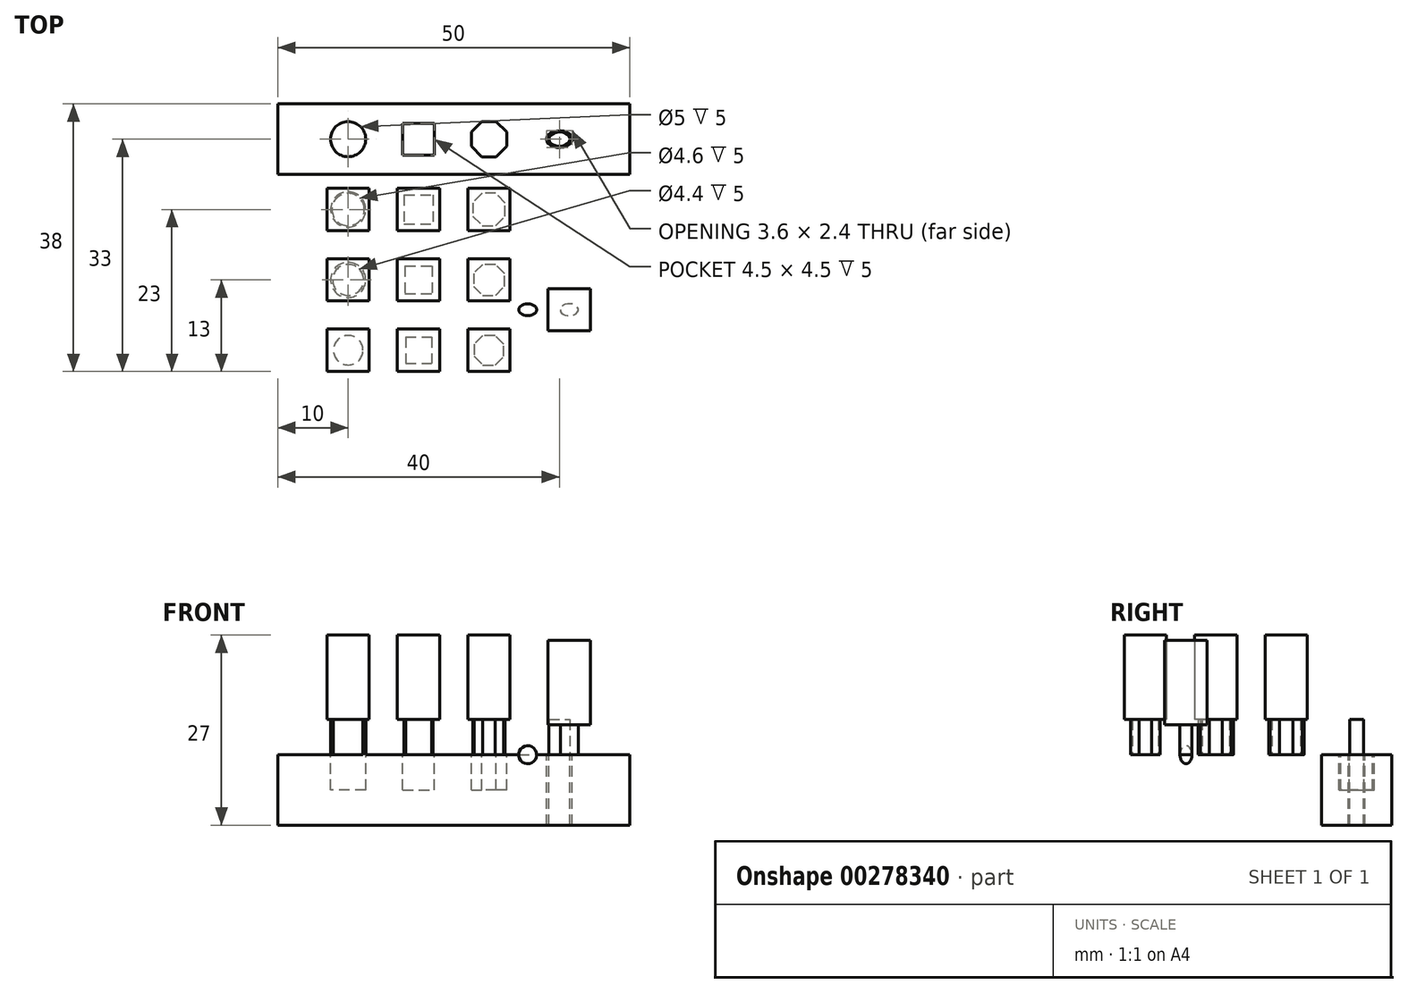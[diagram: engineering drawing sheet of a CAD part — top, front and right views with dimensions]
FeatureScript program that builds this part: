
annotation { "Feature Type Name" : "Feature", "Feature Type Description" : "" }
export const myFeature = defineFeature(function(context is Context, id is Id, definition is map)
    precondition{}
    {
        {
            var Q0;
            Q0=qCreatedBy(makeId("Top.planeOp"),FACE);
            var sketch = newSketch(context, id + "F0", { "sketchPlane" : qUnion([Q0])});
            skLineSegment(sketch, "E0.bottom", {"start": v(0, 0) * mm, "end": v(50, 0) * mm});
            skLineSegment(sketch, "E0.top", {"start": v(0, 10) * mm, "end": v(50, 10) * mm});
            skLineSegment(sketch, "E0.left", {"start": v(0, 0) * mm, "end": v(0, 10) * mm});
            skLineSegment(sketch, "E0.right", {"start": v(50, 0) * mm, "end": v(50, 10) * mm});
            skCircle(sketch, "E1", {"center": v(10, 5) * mm, "radius": 2.5 * mm});
            skPoint(sketch, "E1.centerSnap0", {"position": v(0, 5) * mm});
            skLineSegment(sketch, "E2.bottom", {"start": v(17.75, 2.75) * mm, "end": v(22.25, 2.75) * mm});
            skLineSegment(sketch, "E2.top", {"start": v(17.75, 7.25) * mm, "end": v(22.25, 7.25) * mm});
            skLineSegment(sketch, "E2.left", {"start": v(17.75, 2.75) * mm, "end": v(17.75, 7.25) * mm});
            skLineSegment(sketch, "E2.right", {"start": v(22.25, 2.75) * mm, "end": v(22.25, 7.25) * mm});
            skPoint(sketch, "E2.middle", {"position": v(20, 5) * mm});
            skCircle(sketch, "E3.cCircle", {"center": v(30, 5) * mm, "radius": 2.5 * mm, "construction": true});
            skPoint(sketch, "E3.cCircle.centerSnap0", {"position": v(22.25, 5) * mm});
            skLineSegment(sketch, "E3.0", {"start": v(27.5, 6.04) * mm, "end": v(28.96, 7.5) * mm});
            skLineSegment(sketch, "E3.1", {"start": v(28.96, 7.5) * mm, "end": v(31.04, 7.5) * mm});
            skLineSegment(sketch, "E3.2", {"start": v(31.04, 7.5) * mm, "end": v(32.5, 6.04) * mm});
            skLineSegment(sketch, "E3.3", {"start": v(32.5, 6.04) * mm, "end": v(32.5, 3.96) * mm});
            skLineSegment(sketch, "E3.4", {"start": v(32.5, 3.96) * mm, "end": v(31.04, 2.5) * mm});
            skLineSegment(sketch, "E3.5", {"start": v(31.04, 2.5) * mm, "end": v(28.96, 2.5) * mm});
            skLineSegment(sketch, "E3.6", {"start": v(28.96, 2.5) * mm, "end": v(27.5, 3.96) * mm});
            skLineSegment(sketch, "E3.7", {"start": v(27.5, 3.96) * mm, "end": v(27.5, 6.04) * mm});
            skPoint(sketch, "E3.0.midPoint", {"position": v(28.23, 6.77) * mm});
            skLineSegment(sketch, "E4", {"start": v(40, 2.6) * mm, "end": v(40, 7.41) * mm});
            skCircle(sketch, "E5.MirrorC", {"center": v(10, -5) * mm, "radius": 2.5 * mm});
            skLineSegment(sketch, "E6.MirrorCS", {"start": v(17.75, -2.75) * mm, "end": v(17.75, -7.25) * mm});
            skLineSegment(sketch, "E7.MirrorCS", {"start": v(17.75, -7.25) * mm, "end": v(22.25, -7.25) * mm});
            skLineSegment(sketch, "E8.MirrorCS", {"start": v(22.25, -2.75) * mm, "end": v(22.25, -7.25) * mm});
            skLineSegment(sketch, "E9.MirrorCS", {"start": v(17.75, -2.75) * mm, "end": v(22.25, -2.75) * mm});
            skLineSegment(sketch, "E10.MirrorCS", {"start": v(27.5, -6.04) * mm, "end": v(28.96, -7.5) * mm});
            skLineSegment(sketch, "E11.MirrorCS", {"start": v(28.96, -7.5) * mm, "end": v(31.04, -7.5) * mm});
            skLineSegment(sketch, "E12.MirrorCS", {"start": v(31.04, -7.5) * mm, "end": v(32.5, -6.04) * mm});
            skLineSegment(sketch, "E13.MirrorCS", {"start": v(32.5, -6.04) * mm, "end": v(32.5, -3.96) * mm});
            skLineSegment(sketch, "E14.MirrorCS", {"start": v(32.5, -3.96) * mm, "end": v(31.04, -2.5) * mm});
            skLineSegment(sketch, "E15.MirrorCS", {"start": v(31.04, -2.5) * mm, "end": v(28.96, -2.5) * mm});
            skLineSegment(sketch, "E16.MirrorCS", {"start": v(28.96, -2.5) * mm, "end": v(27.5, -3.96) * mm});
            skLineSegment(sketch, "E17.MirrorCS", {"start": v(27.5, -3.96) * mm, "end": v(27.5, -6.04) * mm});
            skLineSegment(sketch, "E18.0.1.0", {"start": v(31.04, -17.5) * mm, "end": v(32.5, -16.04) * mm});
            skLineSegment(sketch, "E18.0.1.1", {"start": v(17.75, -12.75) * mm, "end": v(17.75, -17.25) * mm});
            skLineSegment(sketch, "E18.0.1.2", {"start": v(17.75, -12.75) * mm, "end": v(22.25, -12.75) * mm});
            skLineSegment(sketch, "E18.0.1.3", {"start": v(27.5, -16.04) * mm, "end": v(28.96, -17.5) * mm});
            skCircle(sketch, "E18.0.1.5", {"center": v(10, -15) * mm, "radius": 2.5 * mm});
            skLineSegment(sketch, "E18.0.1.6", {"start": v(17.75, -17.25) * mm, "end": v(22.25, -17.25) * mm});
            skLineSegment(sketch, "E18.0.1.7", {"start": v(27.5, -13.96) * mm, "end": v(27.5, -16.04) * mm});
            skLineSegment(sketch, "E18.0.1.8", {"start": v(22.25, -12.75) * mm, "end": v(22.25, -17.25) * mm});
            skLineSegment(sketch, "E18.0.1.9", {"start": v(28.96, -17.5) * mm, "end": v(31.04, -17.5) * mm});
            skLineSegment(sketch, "E18.0.1.10", {"start": v(32.5, -16.04) * mm, "end": v(32.5, -13.96) * mm});
            skLineSegment(sketch, "E18.0.1.11", {"start": v(31.04, -12.5) * mm, "end": v(28.96, -12.5) * mm});
            skLineSegment(sketch, "E18.0.1.12", {"start": v(28.96, -12.5) * mm, "end": v(27.5, -13.96) * mm});
            skLineSegment(sketch, "E18.0.1.13", {"start": v(32.5, -13.96) * mm, "end": v(31.04, -12.5) * mm});
            skLineSegment(sketch, "E18.0.2.0", {"start": v(31.04, -27.5) * mm, "end": v(32.5, -26.04) * mm});
            skLineSegment(sketch, "E18.0.2.1", {"start": v(17.75, -22.75) * mm, "end": v(17.75, -27.25) * mm});
            skLineSegment(sketch, "E18.0.2.2", {"start": v(17.75, -22.75) * mm, "end": v(22.25, -22.75) * mm});
            skLineSegment(sketch, "E18.0.2.3", {"start": v(27.5, -26.04) * mm, "end": v(28.96, -27.5) * mm});
            skCircle(sketch, "E18.0.2.5", {"center": v(10, -25) * mm, "radius": 2.5 * mm});
            skLineSegment(sketch, "E18.0.2.6", {"start": v(17.75, -27.25) * mm, "end": v(22.25, -27.25) * mm});
            skLineSegment(sketch, "E18.0.2.7", {"start": v(27.5, -23.96) * mm, "end": v(27.5, -26.04) * mm});
            skLineSegment(sketch, "E18.0.2.8", {"start": v(22.25, -22.75) * mm, "end": v(22.25, -27.25) * mm});
            skLineSegment(sketch, "E18.0.2.9", {"start": v(28.96, -27.5) * mm, "end": v(31.04, -27.5) * mm});
            skLineSegment(sketch, "E18.0.2.10", {"start": v(32.5, -26.04) * mm, "end": v(32.5, -23.96) * mm});
            skLineSegment(sketch, "E18.0.2.11", {"start": v(31.04, -22.5) * mm, "end": v(28.96, -22.5) * mm});
            skLineSegment(sketch, "E18.0.2.12", {"start": v(28.96, -22.5) * mm, "end": v(27.5, -23.96) * mm});
            skLineSegment(sketch, "E18.0.2.13", {"start": v(32.5, -23.96) * mm, "end": v(31.04, -22.5) * mm});
            skCircle(sketch, "E19.0", {"center": v(10, -5) * mm, "radius": 2.3 * mm});
            skCircle(sketch, "E20.0", {"center": v(10, -15) * mm, "radius": 2.2 * mm});
            skCircle(sketch, "E21.0", {"center": v(10, -25) * mm, "radius": 2.1 * mm});
            skLineSegment(sketch, "E22.0", {"start": v(17.95, -2.95) * mm, "end": v(22.05, -2.95) * mm});
            skLineSegment(sketch, "E22.1", {"start": v(17.95, -2.95) * mm, "end": v(17.95, -7.05) * mm});
            skLineSegment(sketch, "E22.2", {"start": v(17.95, -7.05) * mm, "end": v(22.05, -7.05) * mm});
            skLineSegment(sketch, "E22.3", {"start": v(22.05, -2.95) * mm, "end": v(22.05, -7.05) * mm});
            skLineSegment(sketch, "E23.0", {"start": v(18.05, -13.05) * mm, "end": v(18.05, -16.95) * mm});
            skLineSegment(sketch, "E23.1", {"start": v(18.05, -13.05) * mm, "end": v(21.95, -13.05) * mm});
            skLineSegment(sketch, "E23.2", {"start": v(21.95, -13.05) * mm, "end": v(21.95, -16.95) * mm});
            skLineSegment(sketch, "E23.3", {"start": v(18.05, -16.95) * mm, "end": v(21.95, -16.95) * mm});
            skLineSegment(sketch, "E24.0", {"start": v(18.15, -23.15) * mm, "end": v(18.15, -26.85) * mm});
            skLineSegment(sketch, "E24.1", {"start": v(18.15, -23.15) * mm, "end": v(21.85, -23.15) * mm});
            skLineSegment(sketch, "E24.2", {"start": v(21.85, -23.15) * mm, "end": v(21.85, -26.85) * mm});
            skLineSegment(sketch, "E24.3", {"start": v(18.15, -26.85) * mm, "end": v(21.85, -26.85) * mm});
            skLineSegment(sketch, "E25.0", {"start": v(29.05, -7.3) * mm, "end": v(30.95, -7.3) * mm});
            skLineSegment(sketch, "E25.1", {"start": v(27.7, -5.95) * mm, "end": v(29.05, -7.3) * mm});
            skLineSegment(sketch, "E25.2", {"start": v(30.95, -7.3) * mm, "end": v(32.3, -5.95) * mm});
            skLineSegment(sketch, "E25.3", {"start": v(27.7, -4.05) * mm, "end": v(27.7, -5.95) * mm});
            skLineSegment(sketch, "E25.4", {"start": v(32.3, -5.95) * mm, "end": v(32.3, -4.05) * mm});
            skLineSegment(sketch, "E25.5", {"start": v(32.3, -4.05) * mm, "end": v(30.95, -2.7) * mm});
            skLineSegment(sketch, "E25.6", {"start": v(30.95, -2.7) * mm, "end": v(29.05, -2.7) * mm});
            skLineSegment(sketch, "E25.7", {"start": v(29.05, -2.7) * mm, "end": v(27.7, -4.05) * mm});
            skLineSegment(sketch, "E26.0", {"start": v(32.1, -25.87) * mm, "end": v(32.1, -24.13) * mm});
            skLineSegment(sketch, "E26.1", {"start": v(30.87, -27.1) * mm, "end": v(32.1, -25.87) * mm});
            skLineSegment(sketch, "E26.2", {"start": v(32.1, -24.13) * mm, "end": v(30.87, -22.9) * mm});
            skLineSegment(sketch, "E26.3", {"start": v(29.13, -27.1) * mm, "end": v(30.87, -27.1) * mm});
            skLineSegment(sketch, "E26.4", {"start": v(30.87, -22.9) * mm, "end": v(29.13, -22.9) * mm});
            skLineSegment(sketch, "E26.5", {"start": v(29.13, -22.9) * mm, "end": v(27.9, -24.13) * mm});
            skLineSegment(sketch, "E26.6", {"start": v(27.9, -24.13) * mm, "end": v(27.9, -25.87) * mm});
            skLineSegment(sketch, "E26.7", {"start": v(27.9, -25.87) * mm, "end": v(29.13, -27.1) * mm});
            skLineSegment(sketch, "E27.0", {"start": v(29.09, -12.8) * mm, "end": v(27.8, -14.09) * mm});
            skLineSegment(sketch, "E27.1", {"start": v(30.91, -12.8) * mm, "end": v(29.09, -12.8) * mm});
            skLineSegment(sketch, "E27.2", {"start": v(27.8, -14.09) * mm, "end": v(27.8, -15.91) * mm});
            skLineSegment(sketch, "E27.3", {"start": v(32.2, -14.09) * mm, "end": v(30.91, -12.8) * mm});
            skLineSegment(sketch, "E27.4", {"start": v(27.8, -15.91) * mm, "end": v(29.09, -17.2) * mm});
            skLineSegment(sketch, "E27.5", {"start": v(29.09, -17.2) * mm, "end": v(30.91, -17.2) * mm});
            skLineSegment(sketch, "E27.6", {"start": v(30.91, -17.2) * mm, "end": v(32.2, -15.91) * mm});
            skLineSegment(sketch, "E27.7", {"start": v(32.2, -15.91) * mm, "end": v(32.2, -14.09) * mm});
            skEllipse(sketch, "E28", {"center": v(40, 5) * mm, "majorRadius": 1.8 * mm, "minorRadius": 1.2 * mm, "majorAxis": v(-1, 0)});
            skPoint(sketch, "E28.centerSnap0", {"position": v(32.5, 5) * mm});
            skEllipse(sketch, "E29", {"center": v(40, 5) * mm, "majorRadius": 1.5 * mm, "minorRadius": 1 * mm, "majorAxis": v(-1, 0)});
            skSolve(sketch);
        }
        {
            var Q0;
            Q0=makeQuery(id+"F0.imprint","IMPRINT",FACE,{"disambiguationData":[TD([[makeQuery(id+"F0.imprint","IMPRINT",EDGE,{"derivedFrom":sQuery(id+"F0.wireOp",EDGE,"E0.bottom")}),1.0]])]});
            var Q1;
            Q1=makeQuery(id+"F0.imprint","IMPRINT",FACE,{"disambiguationData":[TD([[makeQuery(id+"F0.imprint","IMPRINT",EDGE,{"derivedFrom":sQuery(id+"F0.wireOp",EDGE,"E1")}),1.0]])]});
            var Q2;
            Q2=makeQuery(id+"F0.imprint","IMPRINT",FACE,{"disambiguationData":[TD([[makeQuery(id+"F0.imprint","IMPRINT",EDGE,{"derivedFrom":sQuery(id+"F0.wireOp",EDGE,"E2.bottom")}),1.0]])]});
            var Q3;
            Q3=makeQuery(id+"F0.imprint","IMPRINT",FACE,{"disambiguationData":[TD([[makeQuery(id+"F0.imprint","IMPRINT",EDGE,{"derivedFrom":sQuery(id+"F0.wireOp",EDGE,"E3.0")}),-1.0]])]});
            var Q4;
            {var subQ0=sQuery(id+"F0.wireOp",EDGE,"E4");var subQ1=sQuery(id+"F0.wireOp",EDGE,"KZuQSlj7-sCAI-CJ17-El7u-51rF61ip7YGT");var subQ2=makeQuery(id+"F0.imprint","INTERSECT",VERTEX,{"disambiguationData":[OD(0.0)],"derivedFrom":[subQ1,subQ0]});Q4=makeQuery(id+"F0.imprint","IMPRINT",FACE,{"disambiguationData":[TD([[makeQuery(id+"F0.imprint","IMPRINT",EDGE,{"disambiguationData":[TD([[subQ2,-1.0]])],"derivedFrom":subQ1}),1.0]])]});}
            var Q5;
            {var subQ0=sQuery(id+"F0.wireOp",EDGE,"E4");var subQ1=sQuery(id+"F0.wireOp",EDGE,"KZuQSlj7-sCAI-CJ17-El7u-51rF61ip7YGT");var subQ2=makeQuery(id+"F0.imprint","INTERSECT",VERTEX,{"disambiguationData":[OD(0.0)],"derivedFrom":[subQ1,subQ0]});Q5=makeQuery(id+"F0.imprint","IMPRINT",FACE,{"disambiguationData":[TD([[makeQuery(id+"F0.imprint","IMPRINT",EDGE,{"disambiguationData":[TD([[subQ2,1.0]])],"derivedFrom":subQ1}),-1.0]])]});}
            var Q6;
            {var subQ0=sQuery(id+"F0.wireOp",EDGE,"E4");var subQ1=sQuery(id+"F0.wireOp",EDGE,"KZuQSlj7-sCAI-CJ17-El7u-51rF61ip7YGT");var subQ2=makeQuery(id+"F0.imprint","INTERSECT",VERTEX,{"disambiguationData":[OD(0.0)],"derivedFrom":[subQ1,subQ0]});Q6=makeQuery(id+"F0.imprint","IMPRINT",FACE,{"disambiguationData":[TD([[makeQuery(id+"F0.imprint","IMPRINT",EDGE,{"disambiguationData":[TD([[subQ2,-1.0]])],"derivedFrom":subQ1}),-1.0]])]});}
            var Q7;
            {var subQ0=sQuery(id+"F0.wireOp",EDGE,"E4");var subQ1=sQuery(id+"F0.wireOp",EDGE,"KZuQSlj7-sCAI-CJ17-El7u-51rF61ip7YGT");var subQ2=makeQuery(id+"F0.imprint","INTERSECT",VERTEX,{"disambiguationData":[OD(0.0)],"derivedFrom":[subQ1,subQ0]});Q7=makeQuery(id+"F0.imprint","IMPRINT",FACE,{"disambiguationData":[TD([[makeQuery(id+"F0.imprint","IMPRINT",EDGE,{"disambiguationData":[TD([[subQ2,1.0]])],"derivedFrom":subQ1}),1.0]])]});}
            var Q8;
            {var subQ0=sQuery(id+"F0.wireOp",EDGE,"E29");var subQ1=sQuery(id+"F0.wireOp",EDGE,"E4");var subQ2=makeQuery(id+"F0.imprint","INTERSECT",VERTEX,{"disambiguationData":[OD(0.0)],"derivedFrom":[subQ1,subQ0]});Q8=makeQuery(id+"F0.imprint","IMPRINT",FACE,{"disambiguationData":[TD([[makeQuery(id+"F0.imprint","IMPRINT",EDGE,{"disambiguationData":[TD([[subQ2,-1.0]])],"derivedFrom":subQ1}),-1.0]])]});}
            var Q9;
            {var subQ0=sQuery(id+"F0.wireOp",EDGE,"E29");var subQ1=sQuery(id+"F0.wireOp",EDGE,"E4");var subQ2=makeQuery(id+"F0.imprint","INTERSECT",VERTEX,{"disambiguationData":[OD(0.0)],"derivedFrom":[subQ1,subQ0]});Q9=makeQuery(id+"F0.imprint","IMPRINT",FACE,{"disambiguationData":[TD([[makeQuery(id+"F0.imprint","IMPRINT",EDGE,{"disambiguationData":[TD([[subQ2,-1.0]])],"derivedFrom":subQ1}),1.0]])]});}
            var Q10;
            {var subQ0=sQuery(id+"F0.wireOp",EDGE,"E28");var subQ1=sQuery(id+"F0.wireOp",EDGE,"E4");var subQ2=makeQuery(id+"F0.imprint","INTERSECT",VERTEX,{"disambiguationData":[OD(0.0)],"derivedFrom":[subQ1,subQ0]});Q10=makeQuery(id+"F0.imprint","IMPRINT",FACE,{"disambiguationData":[TD([[makeQuery(id+"F0.imprint","IMPRINT",EDGE,{"disambiguationData":[TD([[subQ2,-1.0]])],"derivedFrom":subQ1}),1.0]])]});}
            var Q11;
            {var subQ0=sQuery(id+"F0.wireOp",EDGE,"E28");var subQ1=sQuery(id+"F0.wireOp",EDGE,"E4");var subQ2=makeQuery(id+"F0.imprint","INTERSECT",VERTEX,{"disambiguationData":[OD(0.0)],"derivedFrom":[subQ1,subQ0]});Q11=makeQuery(id+"F0.imprint","IMPRINT",FACE,{"disambiguationData":[TD([[makeQuery(id+"F0.imprint","IMPRINT",EDGE,{"disambiguationData":[TD([[subQ2,-1.0]])],"derivedFrom":subQ1}),-1.0]])]});}
            extrude(context, id + "F1", {"entities" : qUnion([Q0, Q1, Q2, Q3, Q4, Q5, Q6, Q7, Q8, Q9, Q10, Q11]), "oppositeDirection" : true, "depth" : 10 * mm});
        }
        {
            var Q0;
            Q0=makeQuery(id+"F0.imprint","IMPRINT",FACE,{"disambiguationData":[TD([[makeQuery(id+"F0.imprint","IMPRINT",EDGE,{"derivedFrom":sQuery(id+"F0.wireOp",EDGE,"E1")}),1.0]])]});
            var Q1;
            Q1=makeQuery(id+"F0.imprint","IMPRINT",FACE,{"disambiguationData":[TD([[makeQuery(id+"F0.imprint","IMPRINT",EDGE,{"derivedFrom":sQuery(id+"F0.wireOp",EDGE,"E2.bottom")}),1.0]])]});
            var Q2;
            Q2=makeQuery(id+"F0.imprint","IMPRINT",FACE,{"disambiguationData":[TD([[makeQuery(id+"F0.imprint","IMPRINT",EDGE,{"derivedFrom":sQuery(id+"F0.wireOp",EDGE,"E3.0")}),-1.0]])]});
            extrude(context, id + "F2", {"entities" : qUnion([Q0, Q1, Q2]), "operationType" : NewBodyOperationType.REMOVE, "oppositeDirection" : true, "depth" : 5 * mm});
        }
        {
            var Q0;
            {var subQ0=sQuery(id+"F0.wireOp",EDGE,"E29");var subQ1=sQuery(id+"F0.wireOp",EDGE,"E4");var subQ2=makeQuery(id+"F0.imprint","INTERSECT",VERTEX,{"disambiguationData":[OD(0.0)],"derivedFrom":[subQ1,subQ0]});Q0=makeQuery(id+"F0.imprint","IMPRINT",FACE,{"disambiguationData":[TD([[makeQuery(id+"F0.imprint","IMPRINT",EDGE,{"disambiguationData":[TD([[subQ2,-1.0]])],"derivedFrom":subQ1}),-1.0]])]});}
            var Q1;
            {var subQ0=sQuery(id+"F0.wireOp",EDGE,"E28");var subQ1=sQuery(id+"F0.wireOp",EDGE,"E4");var subQ2=makeQuery(id+"F0.imprint","INTERSECT",VERTEX,{"disambiguationData":[OD(0.0)],"derivedFrom":[subQ1,subQ0]});Q1=makeQuery(id+"F0.imprint","IMPRINT",FACE,{"disambiguationData":[TD([[makeQuery(id+"F0.imprint","IMPRINT",EDGE,{"disambiguationData":[TD([[subQ2,-1.0]])],"derivedFrom":subQ1}),-1.0]])]});}
            var Q2;
            Q2=sQuery(id+"F0.wireOp",EDGE,"E4");
            revolve(context, id + "F3", {"entities" : qUnion([Q0, Q1]), "axis" : qUnion([Q2]), "revolveType" : RevolveType.FULL});
        }
        {
            var Q0;
            {var subQ0=sQuery(id+"F0.wireOp",EDGE,"E29");var subQ1=sQuery(id+"F0.wireOp",EDGE,"E4");var subQ2=makeQuery(id+"F0.imprint","INTERSECT",VERTEX,{"disambiguationData":[OD(0.0)],"derivedFrom":[subQ1,subQ0]});Q0=makeQuery(id+"F0.imprint","IMPRINT",FACE,{"disambiguationData":[TD([[makeQuery(id+"F0.imprint","IMPRINT",EDGE,{"disambiguationData":[TD([[subQ2,-1.0]])],"derivedFrom":subQ1}),1.0]])]});}
            var Q1;
            {var subQ0=sQuery(id+"F0.wireOp",EDGE,"E29");var subQ1=sQuery(id+"F0.wireOp",EDGE,"E4");var subQ2=makeQuery(id+"F0.imprint","INTERSECT",VERTEX,{"disambiguationData":[OD(0.0)],"derivedFrom":[subQ1,subQ0]});Q1=makeQuery(id+"F0.imprint","IMPRINT",FACE,{"disambiguationData":[TD([[makeQuery(id+"F0.imprint","IMPRINT",EDGE,{"disambiguationData":[TD([[subQ2,-1.0]])],"derivedFrom":subQ1}),-1.0]])]});}
            extrude(context, id + "F4", {"entities" : qUnion([Q0, Q1]), "depth" : 5 * mm});
        }
        {
            var Q0;
            Q0=makeQuery(id+"F3.opRevolve","SWEPT_BODY",BODY,{"disambiguationData":[OSD([sQuery(id+"F0.wireOp",EDGE,"E4"),sQuery(id+"F0.wireOp",EDGE,"E28")])]});
            var Q1;
            Q1=makeQuery(id+"F4.opExtrude","SWEPT_BODY",BODY,{"disambiguationData":[OSD([sQuery(id+"F0.wireOp",EDGE,"E29")])]});
            var Q2;
            Q2=sQuery(id+"F0.wireOp",EDGE,"E0.right");
            transform(context, id + "F5", {"entities" : qUnion([Q0, Q1]), "transformType" : TransformType.TRANSLATION_DISTANCE, "transformDirection" : qUnion([Q2]), "distance" : 25 * mm, "oppositeDirection" : true, "makeCopy" : true});
        }
        {
            var Q0;
            Q0=makeQuery(id+"F5.opPattern","COPY",BODY,{"derivedFrom":makeQuery(id+"F4.opExtrude","SWEPT_BODY",BODY,{"disambiguationData":[OSD([sQuery(id+"F0.wireOp",EDGE,"E29")])]}),"instanceName":"1"});
            var Q1;
            Q1=makeQuery(id+"F5.opPattern","COPY",BODY,{"derivedFrom":makeQuery(id+"F3.opRevolve","SWEPT_BODY",BODY,{"disambiguationData":[OSD([sQuery(id+"F0.wireOp",EDGE,"E4"),sQuery(id+"F0.wireOp",EDGE,"E28")])]}),"instanceName":"1"});
            var Q2;
            Q2=sQuery(id+"F0.wireOp",VERTEX,"E18.0.1.5.center");
            transform(context, id + "F6", {"entities" : qUnion([Q0, Q1]), "transformType" : TransformType.SCALE_UNIFORMLY, "scale" : 0.85, "scalePoint" : qUnion([Q2]), "makeCopy" : false});
        }
        {
            var Q0;
            Q0=makeQuery(id+"F5.opPattern","COPY",FACE,{"derivedFrom":makeQuery(id+"F4.opExtrude","CAP_FACE",FACE,{"disambiguationData":[OSD([sQuery(id+"F0.wireOp",EDGE,"E29")])],"isStart":true}),"instanceName":"1"});
            var sketch = newSketch(context, id + "F7", { "sketchPlane" : qUnion([Q0])});
            skEllipticalArc(sketch, "E30.0.0", {"construction": true});
            skLineSegment(sketch, "E31.bottom", {"start": v(33.17, 19.05) * mm, "end": v(35.3, 19.05) * mm});
            skLineSegment(sketch, "E31.top", {"start": v(33.17, 19.45) * mm, "end": v(35.3, 19.45) * mm});
            skLineSegment(sketch, "E31.left", {"start": v(33.17, 19.05) * mm, "end": v(33.17, 19.45) * mm});
            skLineSegment(sketch, "E31.right", {"start": v(37.83, 19.05) * mm, "end": v(37.83, 19.45) * mm});
            skLineSegment(sketch, "E32.bottom", {"start": v(35.7, 17.3) * mm, "end": v(35.3, 17.3) * mm});
            skLineSegment(sketch, "E32.top", {"start": v(35.7, 21.2) * mm, "end": v(35.3, 21.2) * mm});
            skLineSegment(sketch, "E32.left", {"start": v(35.7, 17.3) * mm, "end": v(35.7, 19.05) * mm});
            skLineSegment(sketch, "E32.right", {"start": v(35.3, 17.3) * mm, "end": v(35.3, 19.05) * mm});
            skLineSegment(sketch, "E33.trimOffspring", {"start": v(35.3, 19.45) * mm, "end": v(35.3, 21.2) * mm});
            skLineSegment(sketch, "E34.trimOffspring", {"start": v(35.7, 19.05) * mm, "end": v(37.83, 19.05) * mm});
            skLineSegment(sketch, "E35.trimOffspring", {"start": v(35.7, 19.45) * mm, "end": v(37.83, 19.45) * mm});
            skLineSegment(sketch, "E36.trimOffspring", {"start": v(35.7, 19.45) * mm, "end": v(35.7, 21.2) * mm});
            skEllipticalArc(sketch, "E37.trimOffspring", {"construction": true});
            skEllipticalArc(sketch, "E38.trimOffspring", {"construction": true});
            skEllipticalArc(sketch, "E39.trimOffspring", {"construction": true});
            const initialGuessF7  = {"E30.0.0": [0.0355, 0.01925, -1, 0, 0.001275, 0.00085, 4.869902246591525, 6.0456641363981785], "E37.trimOffspring": [0.0355, 0.01925, -1, 0, 0.001275, 0.00085, 1.7283095930017205, 2.9040714828083063], "E38.trimOffspring": [0.0355, 0.01925, -1, 0, 0.001275, 0.00085, 0.23752117078148682, 1.4132830605880615], "E39.trimOffspring": [0.0355, 0.01925, -1, 0, 0.001275, 0.00085, 3.3791138243712013, 4.554875714177866]};
            skSetInitialGuess(sketch, initialGuessF7);
            skSolve(sketch);
        }
        {
            var Q0;
            {var subQ3=sQuery(id+"F7.wireOp",EDGE,"E32.right");var subQ17=sQuery(id+"F7.wireOp",EDGE,"E31.bottom");var subQ18=makeQuery(id+"F7.imprint","INTERSECT",VERTEX,{"derivedFrom":[subQ17,subQ3]});Q0=makeQuery(id+"F7.imprint","IMPRINT",FACE,{"disambiguationData":[TD([[makeQuery(id+"F7.imprint","IMPRINT",EDGE,{"disambiguationData":[TD([[subQ18,1.0]])],"derivedFrom":subQ17}),1.0]])]});}
            var Q1;
            {var subQ0=sQuery(id+"F7.wireOp",EDGE,"E32.bottom");Q1=makeQuery(id+"F7.imprint","IMPRINT",FACE,{"disambiguationData":[TD([[makeQuery(id+"F7.imprint","IMPRINT",EDGE,{"derivedFrom":subQ0}),-1.0]])]});}
            var Q2;
            {var subQ0=sQuery(id+"F7.wireOp",EDGE,"E31.right");Q2=makeQuery(id+"F7.imprint","IMPRINT",FACE,{"disambiguationData":[TD([[makeQuery(id+"F7.imprint","IMPRINT",EDGE,{"derivedFrom":subQ0}),1.0]])]});}
            var Q3;
            {var subQ0=sQuery(id+"F7.wireOp",EDGE,"E32.top");Q3=makeQuery(id+"F7.imprint","IMPRINT",FACE,{"disambiguationData":[TD([[makeQuery(id+"F7.imprint","IMPRINT",EDGE,{"derivedFrom":subQ0}),1.0]])]});}
            var Q4;
            {var subQ0=sQuery(id+"F7.wireOp",EDGE,"E31.left");Q4=makeQuery(id+"F7.imprint","IMPRINT",FACE,{"disambiguationData":[TD([[makeQuery(id+"F7.imprint","IMPRINT",EDGE,{"derivedFrom":subQ0}),-1.0]])]});}
            extrude(context, id + "F8", {"entities" : qUnion([Q0, Q1, Q2, Q3, Q4]), "depth" : 5 * mm});
        }
        {
            var Q0;
            Q0=makeQuery(id+"F8.opExtrude","SWEPT_BODY",BODY,{"disambiguationData":[OSD([sQuery(id+"F7.wireOp",EDGE,"E31.bottom"),sQuery(id+"F7.wireOp",EDGE,"E31.top"),sQuery(id+"F7.wireOp",EDGE,"E31.left"),sQuery(id+"F7.wireOp",EDGE,"E31.right"),sQuery(id+"F7.wireOp",EDGE,"E32.bottom"),sQuery(id+"F7.wireOp",EDGE,"E32.top"),sQuery(id+"F7.wireOp",EDGE,"E32.left"),sQuery(id+"F7.wireOp",EDGE,"E32.right"),sQuery(id+"F7.wireOp",EDGE,"E33.trimOffspring"),sQuery(id+"F7.wireOp",EDGE,"E34.trimOffspring"),sQuery(id+"F7.wireOp",EDGE,"E35.trimOffspring"),sQuery(id+"F7.wireOp",EDGE,"E36.trimOffspring")])]});
            var Q1;
            Q1=makeQuery(id+"F5.opPattern","COPY",BODY,{"derivedFrom":makeQuery(id+"F4.opExtrude","SWEPT_BODY",BODY,{"disambiguationData":[OSD([sQuery(id+"F0.wireOp",EDGE,"E29")])]}),"instanceName":"1"});
            booleanBodies(context, id + "F9", {"operationType" : BooleanOperationType.SUBTRACTION, "tools" : qUnion([Q0]), "targets" : qUnion([Q1])});
        }
        {
            var Q0;
            Q0=makeQuery(id+"F0.imprint","IMPRINT",FACE,{"disambiguationData":[TD([[makeQuery(id+"F0.imprint","IMPRINT",EDGE,{"derivedFrom":sQuery(id+"F0.wireOp",EDGE,"E25.0")}),1.0]])]});
            var Q1;
            Q1=makeQuery(id+"F0.imprint","IMPRINT",FACE,{"disambiguationData":[TD([[makeQuery(id+"F0.imprint","IMPRINT",EDGE,{"derivedFrom":sQuery(id+"F0.wireOp",EDGE,"E27.0")}),1.0]])]});
            var Q2;
            Q2=makeQuery(id+"F0.imprint","IMPRINT",FACE,{"disambiguationData":[TD([[makeQuery(id+"F0.imprint","IMPRINT",EDGE,{"derivedFrom":sQuery(id+"F0.wireOp",EDGE,"E26.0")}),1.0]])]});
            var Q3;
            Q3=makeQuery(id+"F0.imprint","IMPRINT",FACE,{"disambiguationData":[TD([[makeQuery(id+"F0.imprint","IMPRINT",EDGE,{"derivedFrom":sQuery(id+"F0.wireOp",EDGE,"E24.0")}),1.0]])]});
            var Q4;
            Q4=makeQuery(id+"F0.imprint","IMPRINT",FACE,{"disambiguationData":[TD([[makeQuery(id+"F0.imprint","IMPRINT",EDGE,{"derivedFrom":sQuery(id+"F0.wireOp",EDGE,"E23.0")}),1.0]])]});
            var Q5;
            Q5=makeQuery(id+"F0.imprint","IMPRINT",FACE,{"disambiguationData":[TD([[makeQuery(id+"F0.imprint","IMPRINT",EDGE,{"derivedFrom":sQuery(id+"F0.wireOp",EDGE,"E22.0")}),-1.0]])]});
            var Q6;
            Q6=makeQuery(id+"F0.imprint","IMPRINT",FACE,{"disambiguationData":[TD([[makeQuery(id+"F0.imprint","IMPRINT",EDGE,{"derivedFrom":sQuery(id+"F0.wireOp",EDGE,"E19.0")}),-1.0]])]});
            var Q7;
            Q7=makeQuery(id+"F0.imprint","IMPRINT",FACE,{"disambiguationData":[TD([[makeQuery(id+"F0.imprint","IMPRINT",EDGE,{"derivedFrom":sQuery(id+"F0.wireOp",EDGE,"E20.0")}),-1.0]])]});
            var Q8;
            Q8=makeQuery(id+"F0.imprint","IMPRINT",FACE,{"disambiguationData":[TD([[makeQuery(id+"F0.imprint","IMPRINT",EDGE,{"derivedFrom":sQuery(id+"F0.wireOp",EDGE,"E21.0")}),1.0]])]});
            extrude(context, id + "F10", {"entities" : qUnion([Q0, Q1, Q2, Q3, Q4, Q5, Q6, Q7, Q8]), "depth" : 5 * mm});
        }
        {
            var Q0;
            Q0=makeQuery(id+"F3.opRevolve","SWEPT_BODY",BODY,{"disambiguationData":[OSD([sQuery(id+"F0.wireOp",EDGE,"E4"),sQuery(id+"F0.wireOp",EDGE,"E28")])]});
            transform(context, id + "F11", {"entities" : qUnion([Q0]), "transformType" : TransformType.TRANSLATION_3D, "dx" : 0 * mm, "dy" : 0 * mm, "dz" : -3 * mm, "makeCopy" : false});
        }
        {
            var Q0;
            Q0=makeQuery(id+"F5.opPattern","COPY",BODY,{"derivedFrom":makeQuery(id+"F4.opExtrude","SWEPT_BODY",BODY,{"disambiguationData":[OSD([sQuery(id+"F0.wireOp",EDGE,"E29")])]}),"instanceName":"1"});
            transform(context, id + "F12", {"entities" : qUnion([Q0]), "transformType" : TransformType.TRANSLATION_3D, "dx" : 5.9 * mm, "dy" : 0 * mm, "dz" : 0 * mm, "makeCopy" : false});
        }
        {
            var Q0;
            Q0=makeQuery(id+"F3.opRevolve","SWEPT_BODY",BODY,{"disambiguationData":[OSD([sQuery(id+"F0.wireOp",EDGE,"E4"),sQuery(id+"F0.wireOp",EDGE,"E28")])]});
            var Q1;
            Q1=makeQuery(id+"F1.opExtrude","SWEPT_BODY",BODY,{"disambiguationData":[OSD([sQuery(id+"F0.wireOp",EDGE,"E0.bottom"),sQuery(id+"F0.wireOp",EDGE,"E0.top"),sQuery(id+"F0.wireOp",EDGE,"E0.left"),sQuery(id+"F0.wireOp",EDGE,"E0.right")])]});
            booleanBodies(context, id + "F13", {"operationType" : BooleanOperationType.SUBTRACTION, "tools" : qUnion([Q0]), "targets" : qUnion([Q1])});
        }
        {
            var Q0;
            Q0=makeQuery(id+"F10.opExtrude","CAP_FACE",FACE,{"disambiguationData":[OSD([sQuery(id+"F0.wireOp",EDGE,"E25.0"),sQuery(id+"F0.wireOp",EDGE,"E25.1"),sQuery(id+"F0.wireOp",EDGE,"E25.2"),sQuery(id+"F0.wireOp",EDGE,"E25.3"),sQuery(id+"F0.wireOp",EDGE,"E25.4"),sQuery(id+"F0.wireOp",EDGE,"E25.5"),sQuery(id+"F0.wireOp",EDGE,"E25.6"),sQuery(id+"F0.wireOp",EDGE,"E25.7")])],"isStart":false});
            var sketch = newSketch(context, id + "F14", { "sketchPlane" : qUnion([Q0])});
            skLineSegment(sketch, "E40.0.0", {"start": v(27.9, -24.13) * mm, "end": v(27.9, -25.87) * mm, "construction": true});
            skLineSegment(sketch, "E40.0.1", {"start": v(27.9, -25.87) * mm, "end": v(29.13, -27.1) * mm, "construction": true});
            skLineSegment(sketch, "E40.0.2", {"start": v(29.13, -27.1) * mm, "end": v(30.87, -27.1) * mm, "construction": true});
            skLineSegment(sketch, "E40.0.3", {"start": v(30.87, -27.1) * mm, "end": v(32.1, -25.87) * mm, "construction": true});
            skLineSegment(sketch, "E40.0.4", {"start": v(32.1, -25.87) * mm, "end": v(32.1, -24.13) * mm, "construction": true});
            skLineSegment(sketch, "E40.0.5", {"start": v(32.1, -24.13) * mm, "end": v(30.87, -22.9) * mm, "construction": true});
            skLineSegment(sketch, "E40.0.6", {"start": v(30.87, -22.9) * mm, "end": v(29.13, -22.9) * mm, "construction": true});
            skLineSegment(sketch, "E40.0.7", {"start": v(29.13, -22.9) * mm, "end": v(27.9, -24.13) * mm, "construction": true});
            skLineSegment(sketch, "E41.0.0", {"start": v(18.15, -23.15) * mm, "end": v(18.15, -26.85) * mm, "construction": true});
            skLineSegment(sketch, "E41.0.1", {"start": v(18.15, -26.85) * mm, "end": v(21.85, -26.85) * mm, "construction": true});
            skLineSegment(sketch, "E41.0.2", {"start": v(21.85, -26.85) * mm, "end": v(21.85, -23.15) * mm, "construction": true});
            skLineSegment(sketch, "E41.0.3", {"start": v(21.85, -23.15) * mm, "end": v(18.15, -23.15) * mm, "construction": true});
            skCircle(sketch, "E42.0.0", {"center": v(10, -25) * mm, "radius": 2.1 * mm, "construction": true});
            skCircle(sketch, "E43.0.0", {"center": v(10, -15) * mm, "radius": 2.2 * mm, "construction": true});
            skCircle(sketch, "E44.0.0", {"center": v(10, -5) * mm, "radius": 2.3 * mm, "construction": true});
            skLineSegment(sketch, "E45.0.0", {"start": v(22.05, -7.05) * mm, "end": v(22.05, -2.95) * mm, "construction": true});
            skLineSegment(sketch, "E45.0.1", {"start": v(22.05, -2.95) * mm, "end": v(17.95, -2.95) * mm, "construction": true});
            skLineSegment(sketch, "E45.0.2", {"start": v(17.95, -2.95) * mm, "end": v(17.95, -7.05) * mm, "construction": true});
            skLineSegment(sketch, "E45.0.3", {"start": v(17.95, -7.05) * mm, "end": v(22.05, -7.05) * mm, "construction": true});
            skLineSegment(sketch, "E46.0.0", {"start": v(30.95, -2.7) * mm, "end": v(29.05, -2.7) * mm, "construction": true});
            skLineSegment(sketch, "E46.0.1", {"start": v(29.05, -2.7) * mm, "end": v(27.7, -4.05) * mm, "construction": true});
            skLineSegment(sketch, "E46.0.2", {"start": v(27.7, -4.05) * mm, "end": v(27.7, -5.95) * mm, "construction": true});
            skLineSegment(sketch, "E46.0.3", {"start": v(27.7, -5.95) * mm, "end": v(29.05, -7.3) * mm, "construction": true});
            skLineSegment(sketch, "E46.0.4", {"start": v(29.05, -7.3) * mm, "end": v(30.95, -7.3) * mm, "construction": true});
            skLineSegment(sketch, "E46.0.5", {"start": v(30.95, -7.3) * mm, "end": v(32.3, -5.95) * mm, "construction": true});
            skLineSegment(sketch, "E46.0.6", {"start": v(32.3, -5.95) * mm, "end": v(32.3, -4.05) * mm, "construction": true});
            skLineSegment(sketch, "E46.0.7", {"start": v(32.3, -4.05) * mm, "end": v(30.95, -2.7) * mm, "construction": true});
            skLineSegment(sketch, "E47.0.0", {"start": v(30.91, -17.2) * mm, "end": v(32.2, -15.91) * mm, "construction": true});
            skLineSegment(sketch, "E47.0.1", {"start": v(32.2, -15.91) * mm, "end": v(32.2, -14.09) * mm, "construction": true});
            skLineSegment(sketch, "E47.0.2", {"start": v(32.2, -14.09) * mm, "end": v(30.91, -12.8) * mm, "construction": true});
            skLineSegment(sketch, "E47.0.3", {"start": v(30.91, -12.8) * mm, "end": v(29.09, -12.8) * mm, "construction": true});
            skLineSegment(sketch, "E47.0.4", {"start": v(29.09, -12.8) * mm, "end": v(27.8, -14.09) * mm, "construction": true});
            skLineSegment(sketch, "E47.0.5", {"start": v(27.8, -14.09) * mm, "end": v(27.8, -15.91) * mm, "construction": true});
            skLineSegment(sketch, "E47.0.6", {"start": v(27.8, -15.91) * mm, "end": v(29.09, -17.2) * mm, "construction": true});
            skLineSegment(sketch, "E47.0.7", {"start": v(29.09, -17.2) * mm, "end": v(30.91, -17.2) * mm, "construction": true});
            skLineSegment(sketch, "E48.0.0", {"start": v(18.05, -13.05) * mm, "end": v(18.05, -16.95) * mm, "construction": true});
            skLineSegment(sketch, "E48.0.1", {"start": v(18.05, -16.95) * mm, "end": v(21.95, -16.95) * mm, "construction": true});
            skLineSegment(sketch, "E48.0.2", {"start": v(21.95, -16.95) * mm, "end": v(21.95, -13.05) * mm, "construction": true});
            skLineSegment(sketch, "E48.0.3", {"start": v(21.95, -13.05) * mm, "end": v(18.05, -13.05) * mm, "construction": true});
            skLineSegment(sketch, "E49.bottom", {"start": v(13, -22) * mm, "end": v(7, -22) * mm});
            skLineSegment(sketch, "E49.top", {"start": v(13, -28) * mm, "end": v(7, -28) * mm});
            skLineSegment(sketch, "E49.left", {"start": v(13, -22) * mm, "end": v(13, -28) * mm});
            skLineSegment(sketch, "E49.right", {"start": v(7, -22) * mm, "end": v(7, -28) * mm});
            skLineSegment(sketch, "E50.0.1.0", {"start": v(13, -12) * mm, "end": v(13, -18) * mm});
            skLineSegment(sketch, "E50.0.1.1", {"start": v(13, -12) * mm, "end": v(7, -12) * mm});
            skLineSegment(sketch, "E50.0.1.2", {"start": v(7, -12) * mm, "end": v(7, -18) * mm});
            skLineSegment(sketch, "E50.0.1.3", {"start": v(13, -18) * mm, "end": v(7, -18) * mm});
            skLineSegment(sketch, "E50.0.2.0", {"start": v(13, -2) * mm, "end": v(13, -8) * mm});
            skLineSegment(sketch, "E50.0.2.1", {"start": v(13, -2) * mm, "end": v(7, -2) * mm});
            skLineSegment(sketch, "E50.0.2.2", {"start": v(7, -2) * mm, "end": v(7, -8) * mm});
            skLineSegment(sketch, "E50.0.2.3", {"start": v(13, -8) * mm, "end": v(7, -8) * mm});
            skLineSegment(sketch, "E50.1.0.0", {"start": v(23, -22) * mm, "end": v(23, -28) * mm});
            skLineSegment(sketch, "E50.1.0.1", {"start": v(23, -22) * mm, "end": v(17, -22) * mm});
            skLineSegment(sketch, "E50.1.0.2", {"start": v(17, -22) * mm, "end": v(17, -28) * mm});
            skLineSegment(sketch, "E50.1.0.3", {"start": v(23, -28) * mm, "end": v(17, -28) * mm});
            skLineSegment(sketch, "E50.1.1.0", {"start": v(23, -12) * mm, "end": v(23, -18) * mm});
            skLineSegment(sketch, "E50.1.1.1", {"start": v(23, -12) * mm, "end": v(17, -12) * mm});
            skLineSegment(sketch, "E50.1.1.2", {"start": v(17, -12) * mm, "end": v(17, -18) * mm});
            skLineSegment(sketch, "E50.1.1.3", {"start": v(23, -18) * mm, "end": v(17, -18) * mm});
            skLineSegment(sketch, "E50.1.2.0", {"start": v(23, -2) * mm, "end": v(23, -8) * mm});
            skLineSegment(sketch, "E50.1.2.1", {"start": v(23, -2) * mm, "end": v(17, -2) * mm});
            skLineSegment(sketch, "E50.1.2.2", {"start": v(17, -2) * mm, "end": v(17, -8) * mm});
            skLineSegment(sketch, "E50.1.2.3", {"start": v(23, -8) * mm, "end": v(17, -8) * mm});
            skLineSegment(sketch, "E50.2.0.0", {"start": v(33, -22) * mm, "end": v(33, -28) * mm});
            skLineSegment(sketch, "E50.2.0.1", {"start": v(33, -22) * mm, "end": v(27, -22) * mm});
            skLineSegment(sketch, "E50.2.0.2", {"start": v(27, -22) * mm, "end": v(27, -28) * mm});
            skLineSegment(sketch, "E50.2.0.3", {"start": v(33, -28) * mm, "end": v(27, -28) * mm});
            skLineSegment(sketch, "E50.2.1.0", {"start": v(33, -12) * mm, "end": v(33, -18) * mm});
            skLineSegment(sketch, "E50.2.1.1", {"start": v(33, -12) * mm, "end": v(27, -12) * mm});
            skLineSegment(sketch, "E50.2.1.2", {"start": v(27, -12) * mm, "end": v(27, -18) * mm});
            skLineSegment(sketch, "E50.2.1.3", {"start": v(33, -18) * mm, "end": v(27, -18) * mm});
            skLineSegment(sketch, "E50.2.2.0", {"start": v(33, -2) * mm, "end": v(33, -8) * mm});
            skLineSegment(sketch, "E50.2.2.1", {"start": v(33, -2) * mm, "end": v(27, -2) * mm});
            skLineSegment(sketch, "E50.2.2.2", {"start": v(27, -2) * mm, "end": v(27, -8) * mm});
            skLineSegment(sketch, "E50.2.2.3", {"start": v(33, -8) * mm, "end": v(27, -8) * mm});
            skLineSegment(sketch, "E50.direction1", {"start": v(13, -28) * mm, "end": v(23, -28) * mm, "construction": true});
            skLineSegment(sketch, "E50.direction2", {"start": v(13, -28) * mm, "end": v(13, -18) * mm, "construction": true});
            skPoint(sketch, "E51.middle", {"position": v(41.4, -19.25) * mm});
            skSolve(sketch);
        }
        {
            var Q0;
            Q0=makeQuery(id+"F14.imprint","IMPRINT",FACE,{"disambiguationData":[TD([[makeQuery(id+"F14.imprint","IMPRINT",EDGE,{"derivedFrom":sQuery(id+"F14.wireOp",EDGE,"E50.2.1.0")}),-1.0]])]});
            var Q1;
            Q1=makeQuery(id+"F14.imprint","IMPRINT",FACE,{"disambiguationData":[TD([[makeQuery(id+"F14.imprint","IMPRINT",EDGE,{"derivedFrom":sQuery(id+"F14.wireOp",EDGE,"E50.2.0.0")}),-1.0]])]});
            var Q2;
            Q2=makeQuery(id+"F14.imprint","IMPRINT",FACE,{"disambiguationData":[TD([[makeQuery(id+"F14.imprint","IMPRINT",EDGE,{"derivedFrom":sQuery(id+"F14.wireOp",EDGE,"E50.1.0.0")}),-1.0]])]});
            var Q3;
            Q3=makeQuery(id+"F14.imprint","IMPRINT",FACE,{"disambiguationData":[TD([[makeQuery(id+"F14.imprint","IMPRINT",EDGE,{"derivedFrom":sQuery(id+"F14.wireOp",EDGE,"E49.bottom")}),1.0]])]});
            var Q4;
            Q4=makeQuery(id+"F14.imprint","IMPRINT",FACE,{"disambiguationData":[TD([[makeQuery(id+"F14.imprint","IMPRINT",EDGE,{"derivedFrom":sQuery(id+"F14.wireOp",EDGE,"E50.0.1.0")}),-1.0]])]});
            var Q5;
            Q5=makeQuery(id+"F14.imprint","IMPRINT",FACE,{"disambiguationData":[TD([[makeQuery(id+"F14.imprint","IMPRINT",EDGE,{"derivedFrom":sQuery(id+"F14.wireOp",EDGE,"E50.0.2.0")}),-1.0]])]});
            var Q6;
            Q6=makeQuery(id+"F14.imprint","IMPRINT",FACE,{"disambiguationData":[TD([[makeQuery(id+"F14.imprint","IMPRINT",EDGE,{"derivedFrom":sQuery(id+"F14.wireOp",EDGE,"E50.1.2.0")}),-1.0]])]});
            var Q7;
            Q7=makeQuery(id+"F14.imprint","IMPRINT",FACE,{"disambiguationData":[TD([[makeQuery(id+"F14.imprint","IMPRINT",EDGE,{"derivedFrom":sQuery(id+"F14.wireOp",EDGE,"E50.2.2.0")}),-1.0]])]});
            var Q8;
            Q8=makeQuery(id+"F14.imprint","IMPRINT",FACE,{"disambiguationData":[TD([[makeQuery(id+"F14.imprint","IMPRINT",EDGE,{"derivedFrom":sQuery(id+"F14.wireOp",EDGE,"E50.1.1.0")}),-1.0]])]});
            var Q9;
            Q9=makeQuery(id+"F14.imprint","IMPRINT",FACE,{"disambiguationData":[TD([[makeQuery(id+"F14.imprint","IMPRINT",EDGE,{"derivedFrom":makeQuery(id+"F10.opExtrude","CAP_EDGE",EDGE,{"disambiguationData":[OSD([sQuery(id+"F0.wireOp",EDGE,"E25.0")])],"isStart":false})}),1.0]])]});
            extrude(context, id + "F15", {"entities" : qUnion([Q0, Q1, Q2, Q3, Q4, Q5, Q6, Q7, Q8, Q9]), "operationType" : NewBodyOperationType.ADD, "depth" : 12 * mm});
        }
        {
            var Q0;
            Q0=makeQuery(id+"F5.opPattern","COPY",FACE,{"derivedFrom":makeQuery(id+"F4.opExtrude","CAP_FACE",FACE,{"disambiguationData":[OSD([sQuery(id+"F0.wireOp",EDGE,"E29")])],"isStart":false}),"instanceName":"1"});
            var sketch = newSketch(context, id + "F16", { "sketchPlane" : qUnion([Q0])});
            skEllipse(sketch, "E52.0.0", {"center": v(41.4, -19.25) * mm, "majorRadius": 1.28 * mm, "minorRadius": 0.85 * mm, "majorAxis": v(-1, 0), "construction": true});
            skLineSegment(sketch, "E53.bottom", {"start": v(44.4, -16.25) * mm, "end": v(38.4, -16.25) * mm});
            skLineSegment(sketch, "E53.top", {"start": v(44.4, -22.25) * mm, "end": v(38.4, -22.25) * mm});
            skLineSegment(sketch, "E53.left", {"start": v(44.4, -16.25) * mm, "end": v(44.4, -22.25) * mm});
            skLineSegment(sketch, "E53.right", {"start": v(38.4, -16.25) * mm, "end": v(38.4, -22.25) * mm});
            skSolve(sketch);
        }
        {
            var Q0;
            Q0=makeQuery(id+"F16.imprint","IMPRINT",FACE,{"disambiguationData":[TD([[makeQuery(id+"F16.imprint","IMPRINT",EDGE,{"derivedFrom":sQuery(id+"F16.wireOp",EDGE,"E53.bottom")}),1.0]])]});
            var Q1;
            Q1=makeQuery(id+"F16.imprint","IMPRINT",FACE,{"disambiguationData":[TD([[makeQuery(id+"F16.imprint","IMPRINT",EDGE,{"derivedFrom":makeQuery(id+"F5.opPattern","COPY",EDGE,{"derivedFrom":makeQuery(id+"F4.opExtrude","CAP_EDGE",EDGE,{"disambiguationData":[OSD([sQuery(id+"F0.wireOp",EDGE,"E29")])],"isStart":false}),"instanceName":"1"})}),1.0]])]});
            extrude(context, id + "F17", {"entities" : qUnion([Q0, Q1]), "operationType" : NewBodyOperationType.ADD, "depth" : 12 * mm});
        }
    });
